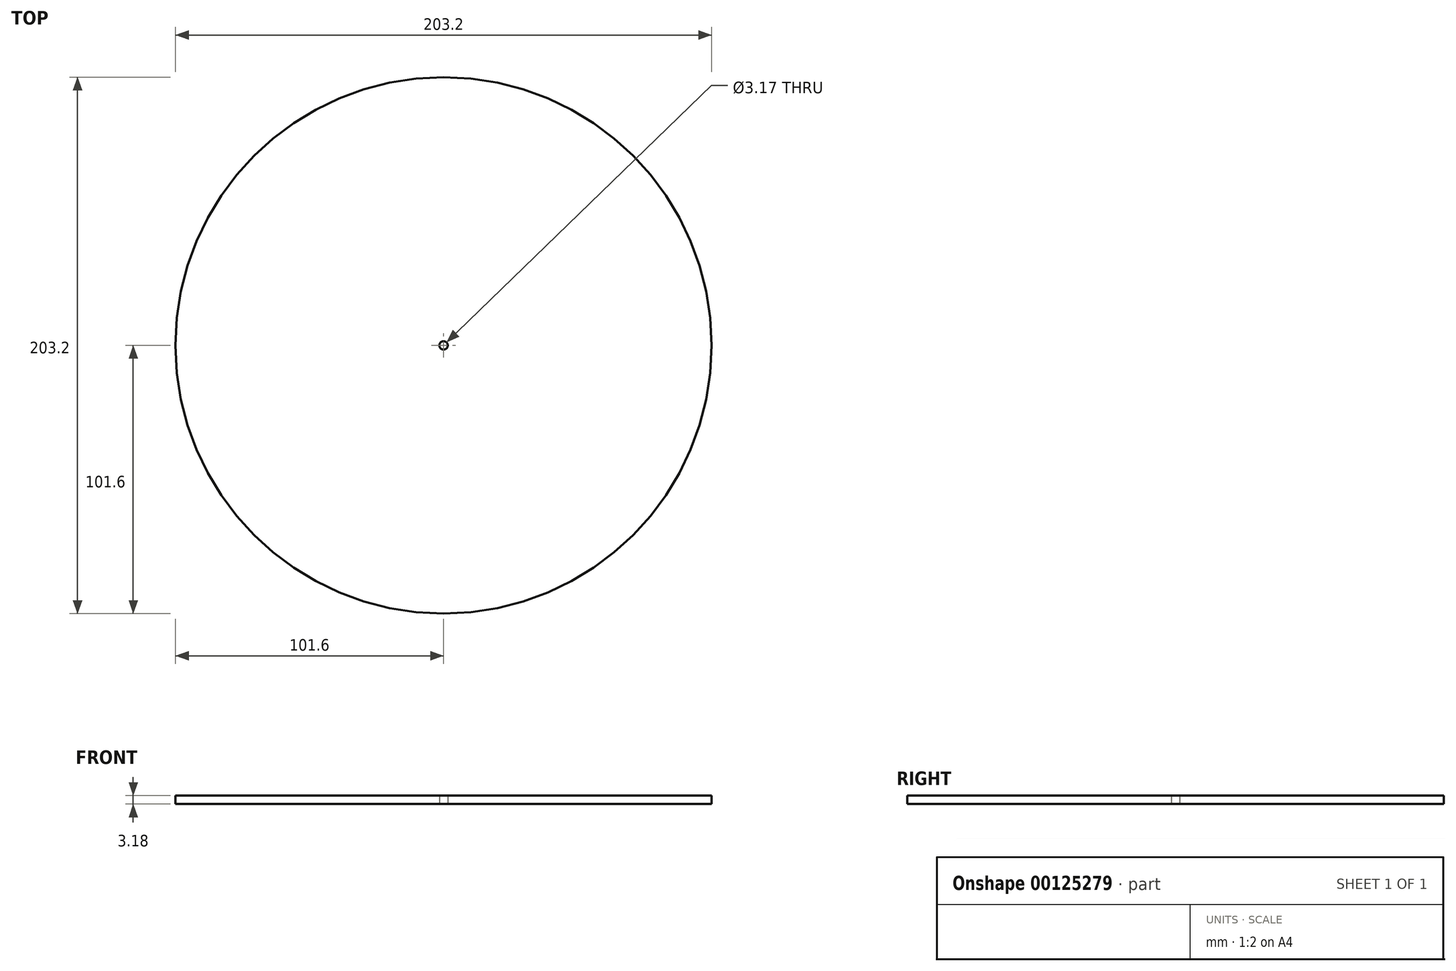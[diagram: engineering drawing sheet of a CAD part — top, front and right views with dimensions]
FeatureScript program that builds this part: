
annotation { "Feature Type Name" : "Feature", "Feature Type Description" : "" }
export const myFeature = defineFeature(function(context is Context, id is Id, definition is map)
    precondition{}
    {
        {
            var Q0;
            Q0=qCreatedBy(makeId("Top.planeOp"),FACE);
            var sketch = newSketch(context, id + "F0", { "sketchPlane" : qUnion([Q0])});
            skCircle(sketch, "E0", {"center": v(0, 0) * mm, "radius": 101.6 * mm});
            skCircle(sketch, "E1", {"center": v(0, 0) * mm, "radius": 1.59 * mm});
            skSolve(sketch);
        }
        {
            var Q0;
            Q0=makeQuery(id+"F0.imprint","IMPRINT",FACE,{"disambiguationData":[TD([[makeQuery(id+"F0.imprint","IMPRINT",EDGE,{"derivedFrom":sQuery(id+"F0.wireOp",EDGE,"E0")}),1.0]])]});
            extrude(context, id + "F1", {"entities" : qUnion([Q0]), "depth" : 3.17 * mm});
        }
    });
